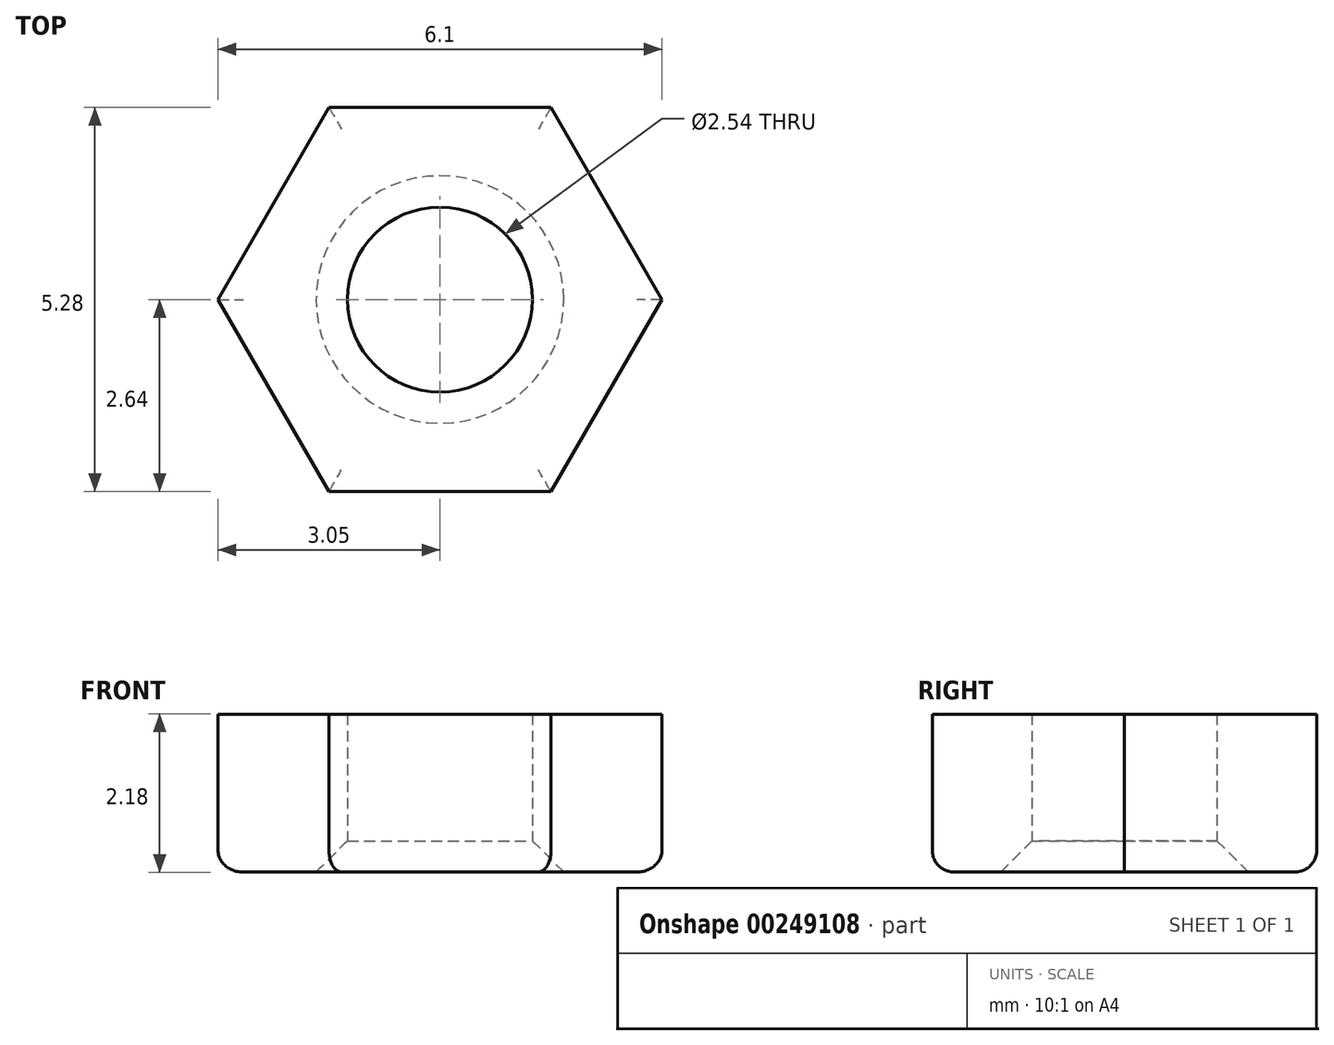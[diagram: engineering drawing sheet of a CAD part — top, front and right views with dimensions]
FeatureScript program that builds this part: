
annotation { "Feature Type Name" : "Feature", "Feature Type Description" : "" }
export const myFeature = defineFeature(function(context is Context, id is Id, definition is map)
    precondition{}
    {
        {
            var Q0;
            Q0=qCreatedBy(makeId("Top.planeOp"),FACE);
            var sketch = newSketch(context, id + "F0", { "sketchPlane" : qUnion([Q0])});
            skCircle(sketch, "E0.cCircle", {"center": v(0, 0) * mm, "radius": 2.64 * mm, "construction": true});
            skLineSegment(sketch, "E0.0", {"start": v(3.05, 0) * mm, "end": v(1.52, -2.64) * mm});
            skLineSegment(sketch, "E0.1", {"start": v(1.52, -2.64) * mm, "end": v(-1.52, -2.64) * mm});
            skLineSegment(sketch, "E0.2", {"start": v(-1.52, -2.64) * mm, "end": v(-3.05, 0) * mm});
            skLineSegment(sketch, "E0.3", {"start": v(-3.05, 0) * mm, "end": v(-1.52, 2.64) * mm});
            skLineSegment(sketch, "E0.4", {"start": v(-1.52, 2.64) * mm, "end": v(1.52, 2.64) * mm});
            skLineSegment(sketch, "E0.5", {"start": v(1.52, 2.64) * mm, "end": v(3.05, 0) * mm});
            skPoint(sketch, "E0.0.midPoint", {"position": v(2.29, -1.32) * mm});
            skSolve(sketch);
        }
        {
            var Q0;
            Q0 = qSketchRegion(id + "F0", true);
            extrude(context, id + "F1", {"entities" : qUnion([Q0]), "endBound" : BoundingType.SYMMETRIC, "depth" : 2.17 * mm});
        }
        {
            var Q0;
            Q0=makeQuery(id+"F1.opExtrude","CAP_FACE",FACE,{"disambiguationData":[OSD([sQuery(id+"F0.wireOp",EDGE,"E0.0"),sQuery(id+"F0.wireOp",EDGE,"E0.1"),sQuery(id+"F0.wireOp",EDGE,"E0.2"),sQuery(id+"F0.wireOp",EDGE,"E0.3"),sQuery(id+"F0.wireOp",EDGE,"E0.4"),sQuery(id+"F0.wireOp",EDGE,"E0.5")])],"isStart":true});
            var sketch = newSketch(context, id + "F2", { "sketchPlane" : qUnion([Q0])});
            skPoint(sketch, "E1", {"position": v(0, 0) * mm});
            skSolve(sketch);
        }
        {
            var Q0;
            Q0=sQuery(id+"F2.wireOp",VERTEX,"E1");
            var Q1;
            Q1=makeQuery(id+"F1.opExtrude","SWEPT_BODY",BODY,{"disambiguationData":[OSD([sQuery(id+"F0.wireOp",EDGE,"E0.0"),sQuery(id+"F0.wireOp",EDGE,"E0.1"),sQuery(id+"F0.wireOp",EDGE,"E0.2"),sQuery(id+"F0.wireOp",EDGE,"E0.3"),sQuery(id+"F0.wireOp",EDGE,"E0.4"),sQuery(id+"F0.wireOp",EDGE,"E0.5")])]});
            hole(context, id + "F3", {"style" : HoleStyle.C_SINK, "endStyle" : HoleEndStyle.THROUGH, "holeDiameter" : 2.54 * mm, "cSinkDiameter" : 3.4 * mm, "cSinkAngle" : 90 * degree, "tappedDepth" : 12 * mm, "tapClearance" : 3, "locations" : qUnion([Q0]), "scope" : qUnion([Q1])});
        }
        {
            var Q0;
            Q0=makeQuery(id+"F1.opExtrude","CAP_EDGE",EDGE,{"disambiguationData":[OSD([sQuery(id+"F0.wireOp",EDGE,"E0.5")])],"isStart":true});
            var Q1;
            Q1=makeQuery(id+"F1.opExtrude","CAP_EDGE",EDGE,{"disambiguationData":[OSD([sQuery(id+"F0.wireOp",EDGE,"E0.0")])],"isStart":true});
            var Q2;
            Q2=makeQuery(id+"F1.opExtrude","CAP_EDGE",EDGE,{"disambiguationData":[OSD([sQuery(id+"F0.wireOp",EDGE,"E0.1")])],"isStart":true});
            var Q3;
            Q3=makeQuery(id+"F1.opExtrude","CAP_EDGE",EDGE,{"disambiguationData":[OSD([sQuery(id+"F0.wireOp",EDGE,"E0.2")])],"isStart":true});
            var Q4;
            Q4=makeQuery(id+"F1.opExtrude","CAP_EDGE",EDGE,{"disambiguationData":[OSD([sQuery(id+"F0.wireOp",EDGE,"E0.3")])],"isStart":true});
            var Q5;
            Q5=makeQuery(id+"F1.opExtrude","CAP_EDGE",EDGE,{"disambiguationData":[OSD([sQuery(id+"F0.wireOp",EDGE,"E0.4")])],"isStart":true});
            fillet(context, id + "F4", {"entities" : qUnion([Q0, Q1, Q2, Q3, Q4, Q5]), "radius" : 0.3 * mm, "tangentPropagation" : true, "allowEdgeOverflow" : false});
        }
    });
